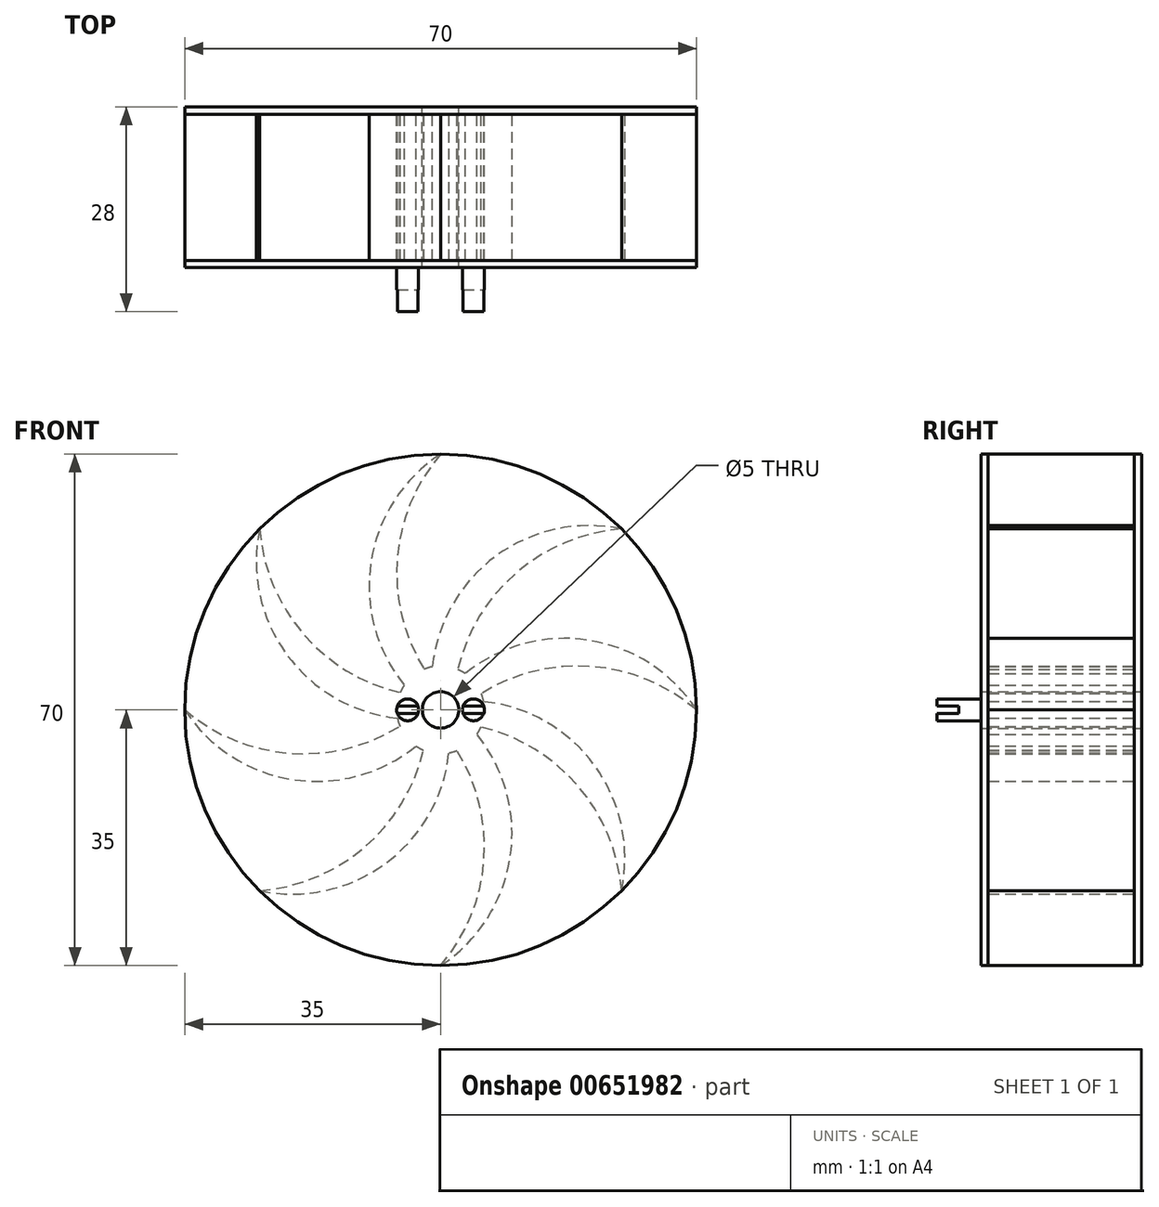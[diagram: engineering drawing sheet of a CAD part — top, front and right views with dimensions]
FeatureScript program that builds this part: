
annotation { "Feature Type Name" : "Feature", "Feature Type Description" : "" }
export const myFeature = defineFeature(function(context is Context, id is Id, definition is map)
    precondition{}
    {
        {
            var Q0;
            Q0=qCreatedBy(makeId("Front.planeOp"),FACE);
            var sketch = newSketch(context, id + "F0", { "sketchPlane" : qUnion([Q0])});
            skCircle(sketch, "E0", {"center": v(0, 0) * mm, "radius": 35 * mm});
            skCircle(sketch, "E1", {"center": v(0, 0) * mm, "radius": 2.5 * mm});
            skArc(sketch, "E2", {"start": v(0, 35) * mm, "mid": v(-5.93, 20.65) * mm, "end": v(-2.24, 5.57) * mm});
            skArc(sketch, "E3", {"start": v(0, 35) * mm, "mid": v(-9.52, 20.29) * mm, "end": v(-4.97, 3.36) * mm});
            skArc(sketch, "E4.1.0", {"start": v(-24.75, 24.75) * mm, "mid": v(-21.07, 7.62) * mm, "end": v(-5.9, -1.13) * mm});
            skArc(sketch, "E4.1.1", {"start": v(-24.75, 24.75) * mm, "mid": v(-18.8, 10.4) * mm, "end": v(-5.52, 2.35) * mm});
            skArc(sketch, "E4.2.0", {"start": v(-35, 0) * mm, "mid": v(-20.29, -9.52) * mm, "end": v(-3.36, -4.97) * mm});
            skArc(sketch, "E4.2.1", {"start": v(-35, 0) * mm, "mid": v(-20.65, -5.93) * mm, "end": v(-5.57, -2.24) * mm});
            skArc(sketch, "E4.3.0", {"start": v(-24.75, -24.75) * mm, "mid": v(-7.62, -21.07) * mm, "end": v(1.13, -5.9) * mm});
            skArc(sketch, "E4.3.1", {"start": v(-24.75, -24.75) * mm, "mid": v(-10.4, -18.8) * mm, "end": v(-2.35, -5.52) * mm});
            skArc(sketch, "E4.4.0", {"start": v(0, -35) * mm, "mid": v(9.52, -20.29) * mm, "end": v(4.97, -3.36) * mm});
            skArc(sketch, "E4.4.1", {"start": v(0, -35) * mm, "mid": v(5.93, -20.65) * mm, "end": v(2.24, -5.57) * mm});
            skArc(sketch, "E4.5.0", {"start": v(24.75, -24.75) * mm, "mid": v(21.07, -7.62) * mm, "end": v(5.9, 1.13) * mm});
            skArc(sketch, "E4.5.1", {"start": v(24.75, -24.75) * mm, "mid": v(18.8, -10.4) * mm, "end": v(5.52, -2.35) * mm});
            skArc(sketch, "E4.6.0", {"start": v(35, 0) * mm, "mid": v(20.29, 9.52) * mm, "end": v(3.36, 4.97) * mm});
            skArc(sketch, "E4.6.1", {"start": v(35, 0) * mm, "mid": v(20.65, 5.93) * mm, "end": v(5.57, 2.24) * mm});
            skArc(sketch, "E4.7.0", {"start": v(24.75, 24.75) * mm, "mid": v(7.62, 21.07) * mm, "end": v(-1.13, 5.9) * mm});
            skArc(sketch, "E4.7.1", {"start": v(24.75, 24.75) * mm, "mid": v(10.4, 18.8) * mm, "end": v(2.35, 5.52) * mm});
            skPoint(sketch, "E5.orphan", {"position": v(-2.2, -1.2) * mm});
            skPoint(sketch, "E6.orphan", {"position": v(-2.5, 0) * mm});
            skPoint(sketch, "E7.orphan", {"position": v(-2.4, 0.7) * mm});
            skPoint(sketch, "E8.orphan", {"position": v(-1.77, 1.77) * mm});
            skPoint(sketch, "E9.orphan", {"position": v(-1.2, 2.2) * mm});
            skPoint(sketch, "E10.orphan", {"position": v(0, 2.5) * mm});
            skPoint(sketch, "E11.orphan", {"position": v(0.7, 2.4) * mm});
            skPoint(sketch, "E12.orphan", {"position": v(1.77, 1.77) * mm});
            skPoint(sketch, "E13.orphan", {"position": v(2.2, 1.2) * mm});
            skPoint(sketch, "E14.orphan", {"position": v(2.5, 0) * mm});
            skPoint(sketch, "E15.orphan", {"position": v(2.4, -0.7) * mm});
            skPoint(sketch, "E16.orphan", {"position": v(1.77, -1.77) * mm});
            skPoint(sketch, "E17.orphan", {"position": v(1.2, -2.2) * mm});
            skPoint(sketch, "E18.orphan", {"position": v(0, -2.5) * mm});
            skPoint(sketch, "E19.orphan", {"position": v(-0.7, -2.4) * mm});
            skPoint(sketch, "E20.orphan", {"position": v(-1.77, -1.77) * mm});
            skArc(sketch, "E21", {"start": v(-5.9, -1.13) * mm, "mid": v(-5.76, -1.7) * mm, "end": v(-5.57, -2.24) * mm});
            skArc(sketch, "E22.trimOffspring", {"start": v(-4.97, 3.36) * mm, "mid": v(-5.27, 2.87) * mm, "end": v(-5.52, 2.35) * mm});
            skArc(sketch, "E23.trimOffspring", {"start": v(-1.13, 5.9) * mm, "mid": v(-1.7, 5.76) * mm, "end": v(-2.24, 5.57) * mm});
            skArc(sketch, "E24.trimOffspring", {"start": v(3.36, 4.97) * mm, "mid": v(2.87, 5.27) * mm, "end": v(2.35, 5.52) * mm});
            skArc(sketch, "E25.trimOffspring", {"start": v(5.9, 1.13) * mm, "mid": v(5.76, 1.7) * mm, "end": v(5.57, 2.24) * mm});
            skArc(sketch, "E26.trimOffspring", {"start": v(4.97, -3.36) * mm, "mid": v(5.27, -2.87) * mm, "end": v(5.52, -2.35) * mm});
            skArc(sketch, "E27.trimOffspring", {"start": v(1.13, -5.9) * mm, "mid": v(1.7, -5.76) * mm, "end": v(2.24, -5.57) * mm});
            skArc(sketch, "E28.trimOffspring", {"start": v(-3.36, -4.97) * mm, "mid": v(-2.87, -5.27) * mm, "end": v(-2.35, -5.52) * mm});
            skSolve(sketch);
        }
        {
            var Q0;
            Q0=makeQuery(id+"F0.imprint","IMPRINT",FACE,{"disambiguationData":[TD([[makeQuery(id+"F0.imprint","IMPRINT",EDGE,{"derivedFrom":sQuery(id+"F0.wireOp",EDGE,"E1")}),-1.0]])]});
            extrude(context, id + "F1", {"entities" : qUnion([Q0]), "depth" : 20 * mm, "offsetDistance" : 25 * mm});
        }
        {
            var Q0;
            Q0 = qSketchRegion(id + "F0", true);
            extrude(context, id + "F2", {"entities" : qUnion([Q0]), "operationType" : NewBodyOperationType.ADD, "oppositeDirection" : true, "depth" : 1 * mm, "offsetDistance" : 25 * mm});
        }
        {
            var Q0;
            Q0=makeQuery(id+"F1.opExtrude","CAP_FACE",FACE,{"disambiguationData":[OSD([sQuery(id+"F0.wireOp",EDGE,"E1"),sQuery(id+"F0.wireOp",EDGE,"E2"),sQuery(id+"F0.wireOp",EDGE,"E3"),sQuery(id+"F0.wireOp",EDGE,"E4.1.0"),sQuery(id+"F0.wireOp",EDGE,"E4.1.1"),sQuery(id+"F0.wireOp",EDGE,"E4.2.0"),sQuery(id+"F0.wireOp",EDGE,"E4.2.1"),sQuery(id+"F0.wireOp",EDGE,"E4.3.0"),sQuery(id+"F0.wireOp",EDGE,"E4.3.1"),sQuery(id+"F0.wireOp",EDGE,"E4.4.0"),sQuery(id+"F0.wireOp",EDGE,"E4.4.1"),sQuery(id+"F0.wireOp",EDGE,"E4.5.0"),sQuery(id+"F0.wireOp",EDGE,"E4.5.1"),sQuery(id+"F0.wireOp",EDGE,"E4.6.0"),sQuery(id+"F0.wireOp",EDGE,"E4.6.1"),sQuery(id+"F0.wireOp",EDGE,"E4.7.0"),sQuery(id+"F0.wireOp",EDGE,"E4.7.1"),sQuery(id+"F0.wireOp",EDGE,"E21"),sQuery(id+"F0.wireOp",EDGE,"E22.trimOffspring"),sQuery(id+"F0.wireOp",EDGE,"E23.trimOffspring"),sQuery(id+"F0.wireOp",EDGE,"E24.trimOffspring"),sQuery(id+"F0.wireOp",EDGE,"E25.trimOffspring"),sQuery(id+"F0.wireOp",EDGE,"E26.trimOffspring"),sQuery(id+"F0.wireOp",EDGE,"E27.trimOffspring"),sQuery(id+"F0.wireOp",EDGE,"E28.trimOffspring")])],"isStart":false});
            var sketch = newSketch(context, id + "F3", { "sketchPlane" : qUnion([Q0])});
            skCircle(sketch, "E29", {"center": v(0, 0) * mm, "radius": 35 * mm});
            skCircle(sketch, "E30", {"center": v(0, 0) * mm, "radius": 2.5 * mm});
            skCircle(sketch, "E31", {"center": v(-4.5, 0) * mm, "radius": 1.5 * mm});
            skCircle(sketch, "E32", {"center": v(4.5, 0) * mm, "radius": 1.5 * mm});
            skSolve(sketch);
        }
        {
            var Q0;
            Q0 = qSketchRegion(id + "F3", true);
            extrude(context, id + "F4", {"entities" : qUnion([Q0]), "operationType" : NewBodyOperationType.ADD, "depth" : 1 * mm, "offsetDistance" : 25 * mm});
        }
        {
            var Q0;
            Q0=makeQuery(id+"F4.boolean.opBoolean","SPLIT",FACE,{"disambiguationData":[TD([makeQuery(id+"F4.opExtrude","SWEPT_FACE",FACE,{"disambiguationData":[OSD([sQuery(id+"F3.wireOp",EDGE,"E32")])]})])],"derivedFrom":makeQuery(id+"F1.opExtrude","CAP_FACE",FACE,{"disambiguationData":[OSD([sQuery(id+"F0.wireOp",EDGE,"E1"),sQuery(id+"F0.wireOp",EDGE,"E2"),sQuery(id+"F0.wireOp",EDGE,"E3"),sQuery(id+"F0.wireOp",EDGE,"E4.1.0"),sQuery(id+"F0.wireOp",EDGE,"E4.1.1"),sQuery(id+"F0.wireOp",EDGE,"E4.2.0"),sQuery(id+"F0.wireOp",EDGE,"E4.2.1"),sQuery(id+"F0.wireOp",EDGE,"E4.3.0"),sQuery(id+"F0.wireOp",EDGE,"E4.3.1"),sQuery(id+"F0.wireOp",EDGE,"E4.4.0"),sQuery(id+"F0.wireOp",EDGE,"E4.4.1"),sQuery(id+"F0.wireOp",EDGE,"E4.5.0"),sQuery(id+"F0.wireOp",EDGE,"E4.5.1"),sQuery(id+"F0.wireOp",EDGE,"E4.6.0"),sQuery(id+"F0.wireOp",EDGE,"E4.6.1"),sQuery(id+"F0.wireOp",EDGE,"E4.7.0"),sQuery(id+"F0.wireOp",EDGE,"E4.7.1"),sQuery(id+"F0.wireOp",EDGE,"E21"),sQuery(id+"F0.wireOp",EDGE,"E22.trimOffspring"),sQuery(id+"F0.wireOp",EDGE,"E23.trimOffspring"),sQuery(id+"F0.wireOp",EDGE,"E24.trimOffspring"),sQuery(id+"F0.wireOp",EDGE,"E25.trimOffspring"),sQuery(id+"F0.wireOp",EDGE,"E26.trimOffspring"),sQuery(id+"F0.wireOp",EDGE,"E27.trimOffspring"),sQuery(id+"F0.wireOp",EDGE,"E28.trimOffspring")])],"isStart":false})});
            var Q1;
            Q1=makeQuery(id+"F4.boolean.opBoolean","SPLIT",FACE,{"disambiguationData":[TD([makeQuery(id+"F4.opExtrude","SWEPT_FACE",FACE,{"disambiguationData":[OSD([sQuery(id+"F3.wireOp",EDGE,"E31")])]})])],"derivedFrom":makeQuery(id+"F1.opExtrude","CAP_FACE",FACE,{"disambiguationData":[OSD([sQuery(id+"F0.wireOp",EDGE,"E1"),sQuery(id+"F0.wireOp",EDGE,"E2"),sQuery(id+"F0.wireOp",EDGE,"E3"),sQuery(id+"F0.wireOp",EDGE,"E4.1.0"),sQuery(id+"F0.wireOp",EDGE,"E4.1.1"),sQuery(id+"F0.wireOp",EDGE,"E4.2.0"),sQuery(id+"F0.wireOp",EDGE,"E4.2.1"),sQuery(id+"F0.wireOp",EDGE,"E4.3.0"),sQuery(id+"F0.wireOp",EDGE,"E4.3.1"),sQuery(id+"F0.wireOp",EDGE,"E4.4.0"),sQuery(id+"F0.wireOp",EDGE,"E4.4.1"),sQuery(id+"F0.wireOp",EDGE,"E4.5.0"),sQuery(id+"F0.wireOp",EDGE,"E4.5.1"),sQuery(id+"F0.wireOp",EDGE,"E4.6.0"),sQuery(id+"F0.wireOp",EDGE,"E4.6.1"),sQuery(id+"F0.wireOp",EDGE,"E4.7.0"),sQuery(id+"F0.wireOp",EDGE,"E4.7.1"),sQuery(id+"F0.wireOp",EDGE,"E21"),sQuery(id+"F0.wireOp",EDGE,"E22.trimOffspring"),sQuery(id+"F0.wireOp",EDGE,"E23.trimOffspring"),sQuery(id+"F0.wireOp",EDGE,"E24.trimOffspring"),sQuery(id+"F0.wireOp",EDGE,"E25.trimOffspring"),sQuery(id+"F0.wireOp",EDGE,"E26.trimOffspring"),sQuery(id+"F0.wireOp",EDGE,"E27.trimOffspring"),sQuery(id+"F0.wireOp",EDGE,"E28.trimOffspring")])],"isStart":false})});
            extrude(context, id + "F5", {"entities" : qUnion([Q0, Q1]), "operationType" : NewBodyOperationType.ADD, "depth" : 7 * mm, "offsetDistance" : 25 * mm});
        }
        {
            var Q0;
            {var subQ0=sQuery(id+"F0.wireOp",EDGE,"E28.trimOffspring");var subQ1=sQuery(id+"F0.wireOp",EDGE,"E27.trimOffspring");var subQ2=sQuery(id+"F0.wireOp",EDGE,"E26.trimOffspring");var subQ3=sQuery(id+"F0.wireOp",EDGE,"E25.trimOffspring");var subQ4=sQuery(id+"F0.wireOp",EDGE,"E24.trimOffspring");var subQ5=sQuery(id+"F0.wireOp",EDGE,"E23.trimOffspring");var subQ6=sQuery(id+"F0.wireOp",EDGE,"E22.trimOffspring");var subQ7=sQuery(id+"F0.wireOp",EDGE,"E21");var subQ8=sQuery(id+"F0.wireOp",EDGE,"E4.7.1");var subQ9=sQuery(id+"F0.wireOp",EDGE,"E4.7.0");var subQ10=sQuery(id+"F0.wireOp",EDGE,"E4.6.1");var subQ11=sQuery(id+"F0.wireOp",EDGE,"E4.6.0");var subQ12=sQuery(id+"F0.wireOp",EDGE,"E4.5.1");var subQ13=sQuery(id+"F0.wireOp",EDGE,"E4.5.0");var subQ14=sQuery(id+"F0.wireOp",EDGE,"E4.4.1");var subQ15=sQuery(id+"F0.wireOp",EDGE,"E4.4.0");var subQ16=sQuery(id+"F0.wireOp",EDGE,"E4.3.1");var subQ17=sQuery(id+"F0.wireOp",EDGE,"E4.3.0");var subQ18=sQuery(id+"F0.wireOp",EDGE,"E4.2.1");var subQ19=sQuery(id+"F0.wireOp",EDGE,"E4.2.0");var subQ20=sQuery(id+"F0.wireOp",EDGE,"E4.1.1");var subQ21=sQuery(id+"F0.wireOp",EDGE,"E4.1.0");var subQ22=sQuery(id+"F0.wireOp",EDGE,"E3");var subQ23=sQuery(id+"F0.wireOp",EDGE,"E2");var subQ24=sQuery(id+"F0.wireOp",EDGE,"E1");Q0=makeQuery(id+"F5.opExtrude","CAP_FACE",FACE,{"disambiguationData":[OSD([subQ24,subQ23,subQ22,subQ21,subQ20,subQ19,subQ18,subQ17,subQ16,subQ15,subQ14,subQ13,subQ12,subQ11,subQ10,subQ9,subQ8,subQ7,subQ6,subQ5,subQ4,subQ3,subQ2,subQ1,subQ0]),TDD([makeQuery(id+"F4.boolean.opBoolean","SPLIT",FACE,{"disambiguationData":[TD([makeQuery(id+"F4.opExtrude","SWEPT_FACE",FACE,{"disambiguationData":[OSD([sQuery(id+"F3.wireOp",EDGE,"E31")])]})])],"derivedFrom":makeQuery(id+"F1.opExtrude","CAP_FACE",FACE,{"disambiguationData":[OSD([subQ24,subQ23,subQ22,subQ21,subQ20,subQ19,subQ18,subQ17,subQ16,subQ15,subQ14,subQ13,subQ12,subQ11,subQ10,subQ9,subQ8,subQ7,subQ6,subQ5,subQ4,subQ3,subQ2,subQ1,subQ0])],"isStart":false})})])],"isStart":false});}
            var sketch = newSketch(context, id + "F6", { "sketchPlane" : qUnion([Q0])});
            skLineSegment(sketch, "E33.bottom", {"start": v(-6, 0.5) * mm, "end": v(-3, 0.5) * mm});
            skLineSegment(sketch, "E33.top", {"start": v(-6, -0.5) * mm, "end": v(-3, -0.5) * mm});
            skLineSegment(sketch, "E33.left", {"start": v(-6, 0.5) * mm, "end": v(-6, -0.5) * mm});
            skLineSegment(sketch, "E33.right", {"start": v(-3, 0.5) * mm, "end": v(-3, -0.5) * mm});
            skPoint(sketch, "E33.middle", {"position": v(-4.5, 0) * mm});
            skSolve(sketch);
        }
        {
            var Q0;
            {var subQ0=sQuery(id+"F0.wireOp",EDGE,"E28.trimOffspring");var subQ1=sQuery(id+"F0.wireOp",EDGE,"E27.trimOffspring");var subQ2=sQuery(id+"F0.wireOp",EDGE,"E26.trimOffspring");var subQ3=sQuery(id+"F0.wireOp",EDGE,"E25.trimOffspring");var subQ4=sQuery(id+"F0.wireOp",EDGE,"E24.trimOffspring");var subQ5=sQuery(id+"F0.wireOp",EDGE,"E23.trimOffspring");var subQ6=sQuery(id+"F0.wireOp",EDGE,"E22.trimOffspring");var subQ7=sQuery(id+"F0.wireOp",EDGE,"E21");var subQ8=sQuery(id+"F0.wireOp",EDGE,"E4.7.1");var subQ9=sQuery(id+"F0.wireOp",EDGE,"E4.7.0");var subQ10=sQuery(id+"F0.wireOp",EDGE,"E4.6.1");var subQ11=sQuery(id+"F0.wireOp",EDGE,"E4.6.0");var subQ12=sQuery(id+"F0.wireOp",EDGE,"E4.5.1");var subQ13=sQuery(id+"F0.wireOp",EDGE,"E4.5.0");var subQ14=sQuery(id+"F0.wireOp",EDGE,"E4.4.1");var subQ15=sQuery(id+"F0.wireOp",EDGE,"E4.4.0");var subQ16=sQuery(id+"F0.wireOp",EDGE,"E4.3.1");var subQ17=sQuery(id+"F0.wireOp",EDGE,"E4.3.0");var subQ18=sQuery(id+"F0.wireOp",EDGE,"E4.2.1");var subQ19=sQuery(id+"F0.wireOp",EDGE,"E4.2.0");var subQ20=sQuery(id+"F0.wireOp",EDGE,"E4.1.1");var subQ21=sQuery(id+"F0.wireOp",EDGE,"E4.1.0");var subQ22=sQuery(id+"F0.wireOp",EDGE,"E3");var subQ23=sQuery(id+"F0.wireOp",EDGE,"E2");var subQ24=sQuery(id+"F0.wireOp",EDGE,"E1");Q0=makeQuery(id+"F5.opExtrude","CAP_FACE",FACE,{"disambiguationData":[OSD([subQ24,subQ23,subQ22,subQ21,subQ20,subQ19,subQ18,subQ17,subQ16,subQ15,subQ14,subQ13,subQ12,subQ11,subQ10,subQ9,subQ8,subQ7,subQ6,subQ5,subQ4,subQ3,subQ2,subQ1,subQ0]),TDD([makeQuery(id+"F4.boolean.opBoolean","SPLIT",FACE,{"disambiguationData":[TD([makeQuery(id+"F4.opExtrude","SWEPT_FACE",FACE,{"disambiguationData":[OSD([sQuery(id+"F3.wireOp",EDGE,"E32")])]})])],"derivedFrom":makeQuery(id+"F1.opExtrude","CAP_FACE",FACE,{"disambiguationData":[OSD([subQ24,subQ23,subQ22,subQ21,subQ20,subQ19,subQ18,subQ17,subQ16,subQ15,subQ14,subQ13,subQ12,subQ11,subQ10,subQ9,subQ8,subQ7,subQ6,subQ5,subQ4,subQ3,subQ2,subQ1,subQ0])],"isStart":false})})])],"isStart":false});}
            var sketch = newSketch(context, id + "F7", { "sketchPlane" : qUnion([Q0])});
            skLineSegment(sketch, "E34.bottom", {"start": v(3, 0.5) * mm, "end": v(6, 0.5) * mm});
            skLineSegment(sketch, "E34.top", {"start": v(3, -0.5) * mm, "end": v(6, -0.5) * mm});
            skLineSegment(sketch, "E34.left", {"start": v(3, 0.5) * mm, "end": v(3, -0.5) * mm});
            skLineSegment(sketch, "E34.right", {"start": v(6, 0.5) * mm, "end": v(6, -0.5) * mm});
            skPoint(sketch, "E34.middle", {"position": v(4.5, 0) * mm});
            skSolve(sketch);
        }
        {
            var Q0;
            {var subQ0=sQuery(id+"F6.wireOp",EDGE,"E33.bottom");var subQ1=makeQuery(id+"F5.opExtrude","CAP_EDGE",EDGE,{"disambiguationData":[OSD([sQuery(id+"F3.wireOp",EDGE,"E31")])],"isStart":false});var subQ4=makeQuery(id+"F6.imprint","INTERSECT",VERTEX,{"disambiguationData":[OD(0.0)],"derivedFrom":[subQ1,subQ0]});Q0=makeQuery(id+"F6.imprint","IMPRINT",FACE,{"disambiguationData":[TD([[makeQuery(id+"F6.imprint","IMPRINT",EDGE,{"disambiguationData":[TD([[subQ4,-1.0]])],"derivedFrom":subQ0}),-1.0]])]});}
            var Q1;
            {var subQ0=sQuery(id+"F7.wireOp",EDGE,"E34.bottom");var subQ1=makeQuery(id+"F5.opExtrude","CAP_EDGE",EDGE,{"disambiguationData":[OSD([sQuery(id+"F3.wireOp",EDGE,"E32")])],"isStart":false});var subQ4=makeQuery(id+"F7.imprint","INTERSECT",VERTEX,{"disambiguationData":[OD(0.0)],"derivedFrom":[subQ1,subQ0]});Q1=makeQuery(id+"F7.imprint","IMPRINT",FACE,{"disambiguationData":[TD([[makeQuery(id+"F7.imprint","IMPRINT",EDGE,{"disambiguationData":[TD([[subQ4,-1.0]])],"derivedFrom":subQ0}),-1.0]])]});}
            extrude(context, id + "F8", {"entities" : qUnion([Q0, Q1]), "operationType" : NewBodyOperationType.REMOVE, "oppositeDirection" : true, "depth" : 3 * mm, "offsetDistance" : 25 * mm});
        }
    });
